# Revit family: Legrand_Lighting_Management_KNX_Presence_Sensor_Wall
name_source: partatom
category: Dispositifs d'éclairage
units: mm (PartAtom-declared; Revit-internal decimal feet)

## family parameters
Conserver l'orientation des annotations = Oui
Cote de connecteur circulaire = Utiliser le diamètre
Couper avec des vides une fois chargée = Non
Hôte = Face
Partagée = Non
Point de calcul de pièce = Non
Type d'élément = Normal

## types (2) — shared parameters
Alarm function = Non
Collecteur de terre = Non
Colour = White
Constant light control = Oui
Cosses d'artère secondaire = Non
Dim function with dimmer basic element = Non
Elévation par défaut = 2500 mm
Fabricant = Legrand
Forced switch off = Non
General Conditions of Use = https://export.legrand.com
HVAC-control = Non
Liaison neutre = Non
Max. duty cycle (mn) = 18
Maximum mounting height (m) = 2.5
Min. switch-on time (s) = 5
Model = Movement sensor
Mounting method = Surface mounted (plaster)
RAL-number (akin) = 9003
Remote operation = Non
Response value luminosity adjustable = Oui
Response value sensitivity adjustable = Oui
Substation input = Non
Suitable for wireless transmission = Non
URL = http://www.legrandoc.com
zero-valued in all types: Detection angle horizontal (MIN) (°), Frequency (MAX) (Hz), Frequency (MIN) (Hz), Max. starting current (A), Max. switching power (W), Nominal voltage (V), Response value luminosity (MAX) (lx), Response value luminosity (MIN) (lx), Temperature (MAX) (°C), Temperature (MIN) (°C)

## per-type parameters (varying)
| type | Description | Detection angle horizontal (MAX) (°) | Diameter detection range on floor (m) | Dual-tech KNX mural 180° | Max. transmission range frontally (m) | Max. transmission range sideways (m) | Modèle | PIR KNX mural 270°+180° |
| Dual-tech KNX wall 180° | BUS/KNX presence sensor - surface mounting - IP 42 - 180° IR & ultrasound - 8 m | 180 | 6 | Oui | 12 | 3 | 048920 | Non |
| PIR KNX wall 270°+180° | BUS/KNX motion sensor - surface mounting - IP 55 - 270° IR - range 20 m | 270 | 10 | Non | 15 | 5 | 048921 | Oui |

## geometry (parser evidence)
native form markers: Blend x10
no freeform markers — native parametric forms only
